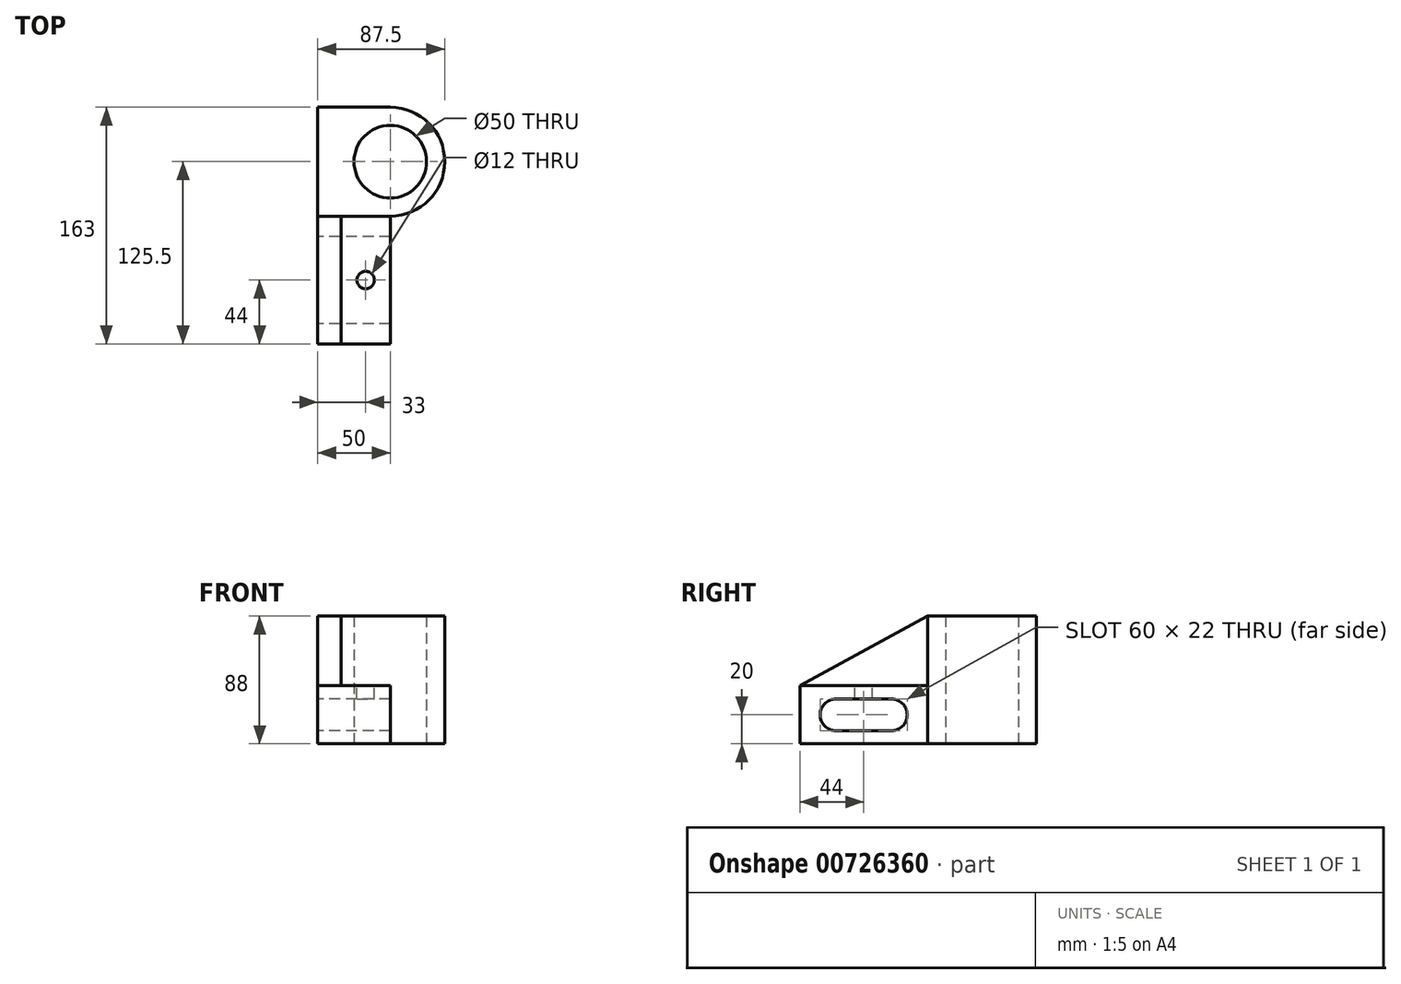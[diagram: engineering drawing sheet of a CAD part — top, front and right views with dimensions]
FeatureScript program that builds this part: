
annotation { "Feature Type Name" : "Feature", "Feature Type Description" : "" }
export const myFeature = defineFeature(function(context is Context, id is Id, definition is map)
    precondition{}
    {
        {
            var Q0;
            Q0=qCreatedBy(makeId("Top.planeOp"),FACE);
            var sketch = newSketch(context, id + "F0", { "sketchPlane" : qUnion([Q0])});
            skLineSegment(sketch, "E0.bottom", {"start": v(0, 0) * mm, "end": v(50, 0) * mm});
            skLineSegment(sketch, "E0.top", {"start": v(0, 75) * mm, "end": v(50, 75) * mm});
            skLineSegment(sketch, "E0.left", {"start": v(0, 0) * mm, "end": v(0, 75) * mm});
            skArc(sketch, "E1", {"start": v(50, 0) * mm, "mid": v(87.5, 37.5) * mm, "end": v(50, 75) * mm});
            skCircle(sketch, "E2", {"center": v(50, 37.5) * mm, "radius": 25 * mm});
            skSolve(sketch);
        }
        {
            var Q0;
            Q0 = qSketchRegion(id + "F0", true);
            extrude(context, id + "F1", {"entities" : qUnion([Q0]), "depth" : 88 * mm, "offsetDistance" : 25 * mm});
        }
        {
            var Q0;
            Q0=qCreatedBy(makeId("Right.planeOp"),FACE);
            var sketch = newSketch(context, id + "F2", { "sketchPlane" : qUnion([Q0])});
            skLineSegment(sketch, "E3.bottom", {"start": v(0, 0) * mm, "end": v(-88, 0) * mm});
            skLineSegment(sketch, "E3.top", {"start": v(0, 40) * mm, "end": v(-88, 40) * mm});
            skLineSegment(sketch, "E3.left", {"start": v(0, 0) * mm, "end": v(0, 40) * mm});
            skLineSegment(sketch, "E3.right", {"start": v(-88, 0) * mm, "end": v(-88, 40) * mm});
            skLineSegment(sketch, "E4", {"start": v(0, 0) * mm, "end": v(-25, 0) * mm});
            skArc(sketch, "E5", {"start": v(-25, 9) * mm, "mid": v(-14, 20) * mm, "end": v(-25, 31) * mm});
            skArc(sketch, "E6", {"start": v(-63, 31) * mm, "mid": v(-74, 20) * mm, "end": v(-63, 9) * mm});
            skLineSegment(sketch, "E7", {"start": v(-25, 31) * mm, "end": v(-63, 31) * mm});
            skLineSegment(sketch, "E8", {"start": v(-63, 9) * mm, "end": v(-25, 9) * mm});
            skSolve(sketch);
        }
        {
            var Q0;
            Q0 = qSketchRegion(id + "F2", true);
            extrude(context, id + "F3", {"entities" : qUnion([Q0]), "operationType" : NewBodyOperationType.ADD, "depth" : 50 * mm, "offsetDistance" : 25 * mm});
        }
        {
            var Q0;
            Q0=qCreatedBy(makeId("Right.planeOp"),FACE);
            var sketch = newSketch(context, id + "F4", { "sketchPlane" : qUnion([Q0])});
            skLineSegment(sketch, "E9", {"start": v(0, 40) * mm, "end": v(0, 88) * mm});
            skLineSegment(sketch, "E10", {"start": v(0, 40) * mm, "end": v(-88, 40) * mm});
            skLineSegment(sketch, "E11", {"start": v(-88, 40) * mm, "end": v(0, 88) * mm});
            skSolve(sketch);
        }
        {
            var Q0;
            Q0 = qSketchRegion(id + "F4", true);
            extrude(context, id + "F5", {"entities" : qUnion([Q0]), "operationType" : NewBodyOperationType.ADD, "depth" : 16 * mm, "offsetDistance" : 25 * mm});
        }
        {
            var Q0;
            Q0=makeQuery(id+"F3.opExtrude","SWEPT_FACE",FACE,{"disambiguationData":[OSD([sQuery(id+"F2.wireOp",EDGE,"E3.top")])]});
            var sketch = newSketch(context, id + "F6", { "sketchPlane" : qUnion([Q0])});
            skLineSegment(sketch, "E12", {"start": v(39, -44) * mm, "end": v(33, -44) * mm});
            skCircle(sketch, "E13", {"center": v(33, -44) * mm, "radius": 6 * mm});
            skSolve(sketch);
        }
        {
            var Q0;
            Q0=makeQuery(id+"F6.imprint","IMPRINT",FACE,{"disambiguationData":[TD([[makeQuery(id+"F6.imprint","IMPRINT",EDGE,{"derivedFrom":sQuery(id+"F6.wireOp",EDGE,"E13")}),-1.0]])]});
            var sketch = newSketch(context, id + "F7", { "sketchPlane" : qUnion([Q0])});
            skSolve(sketch);
        }
        {
            var Q0;
            Q0=makeQuery(id+"F7.imprint","IMPRINT",FACE,{"disambiguationData":[TD([[makeQuery(id+"F7.imprint","IMPRINT",EDGE,{"derivedFrom":makeQuery(id+"F6.imprint","IMPRINT",EDGE,{"derivedFrom":sQuery(id+"F6.wireOp",EDGE,"E13")})}),1.0]])]});
            extrude(context, id + "F8", {"entities" : qUnion([Q0]), "operationType" : NewBodyOperationType.REMOVE, "endBound" : BoundingType.UP_TO_NEXT, "oppositeDirection" : true, "depth" : 25 * mm, "offsetDistance" : 25 * mm});
        }
    });
